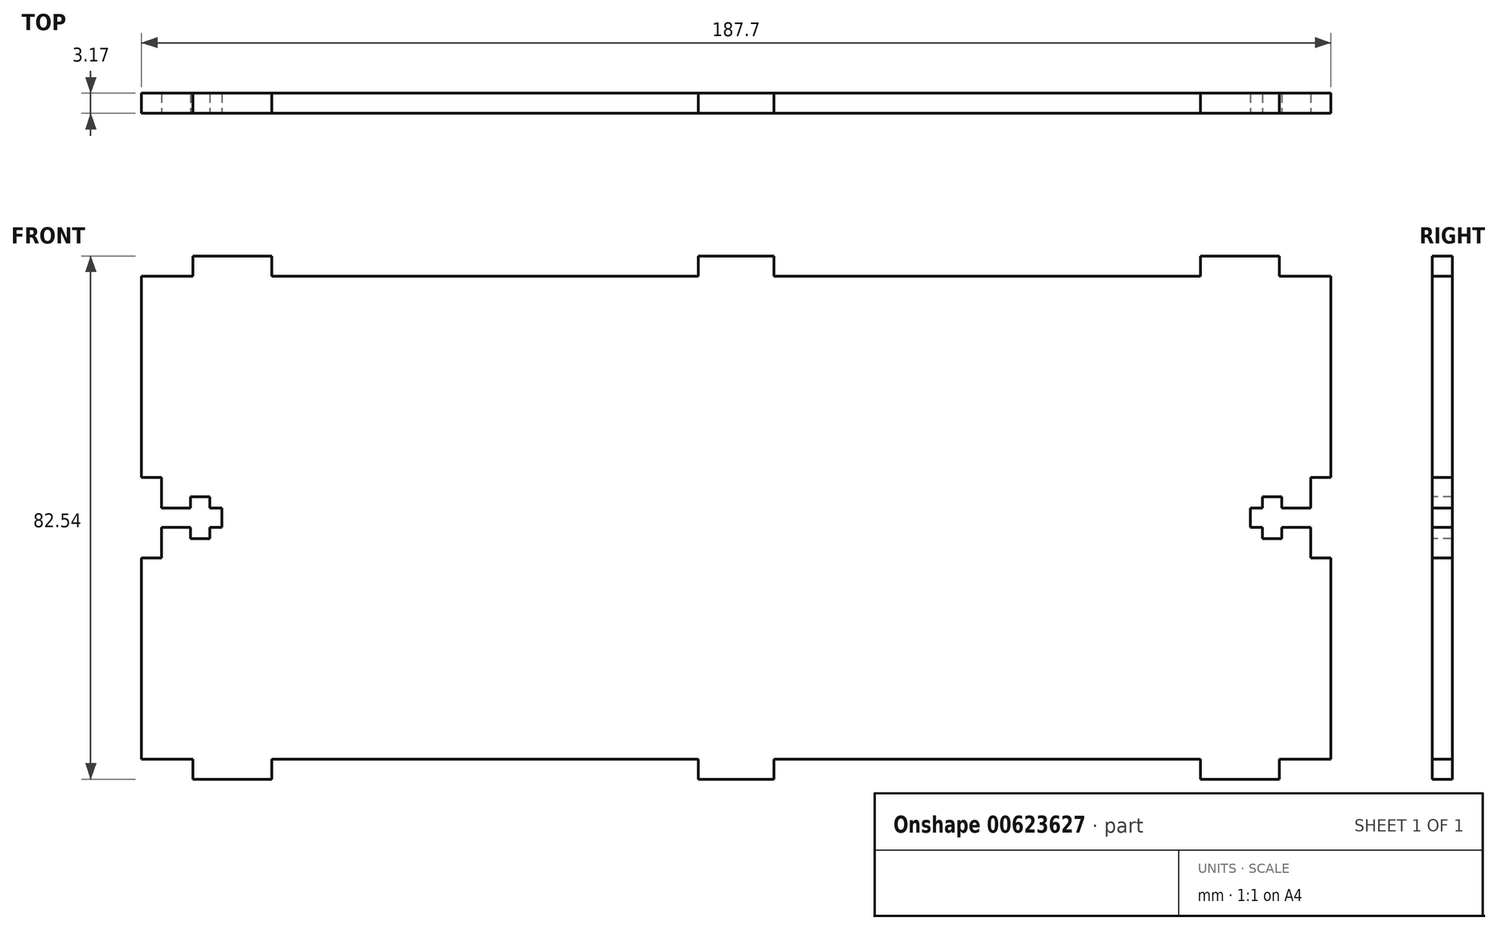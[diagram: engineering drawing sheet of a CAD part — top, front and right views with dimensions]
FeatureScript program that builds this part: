
annotation { "Feature Type Name" : "Feature", "Feature Type Description" : "" }
export const myFeature = defineFeature(function(context is Context, id is Id, definition is map)
    precondition{}
    {
        {
            var Q0;
            Q0=qCreatedBy(makeId("Front.planeOp"),FACE);
            var sketch = newSketch(context, id + "F0", { "sketchPlane" : qUnion([Q0])});
            skLineSegment(sketch, "E0.bottom", {"start": v(93.85, -41.27) * mm, "end": v(-93.85, -41.28) * mm});
            skLineSegment(sketch, "E0.top", {"start": v(93.85, 41.28) * mm, "end": v(-93.85, 41.27) * mm});
            skLineSegment(sketch, "E0.left", {"start": v(93.85, -41.27) * mm, "end": v(93.85, 41.28) * mm});
            skLineSegment(sketch, "E0.right", {"start": v(-93.85, -41.28) * mm, "end": v(-93.85, 41.27) * mm});
            skPoint(sketch, "E0.middle", {"position": v(0, 0) * mm});
            skSolve(sketch);
        }
        {
            var Q0;
            Q0 = qSketchRegion(id + "F0", true);
            extrude(context, id + "F1", {"entities" : qUnion([Q0]), "depth" : 3.17 * mm, "offsetDistance" : 25.4 * mm});
        }
        {
            var Q0;
            Q0=makeQuery(id+"F1.opExtrude","CAP_FACE",FACE,{"disambiguationData":[OSD([sQuery(id+"F0.wireOp",EDGE,"E0.bottom"),sQuery(id+"F0.wireOp",EDGE,"E0.top"),sQuery(id+"F0.wireOp",EDGE,"E0.left"),sQuery(id+"F0.wireOp",EDGE,"E0.right")])],"isStart":false});
            var sketch = newSketch(context, id + "F2", { "sketchPlane" : qUnion([Q0])});
            skLineSegment(sketch, "E1.bottom", {"start": v(-93.85, 41.27) * mm, "end": v(-85.73, 41.27) * mm});
            skLineSegment(sketch, "E1.top", {"start": v(-93.85, 38.1) * mm, "end": v(-85.73, 38.1) * mm});
            skLineSegment(sketch, "E1.left", {"start": v(-93.85, 41.27) * mm, "end": v(-93.85, 38.1) * mm});
            skLineSegment(sketch, "E1.right", {"start": v(-85.73, 41.27) * mm, "end": v(-85.73, 38.1) * mm});
            skLineSegment(sketch, "E2.bottom", {"start": v(-73.28, 41.27) * mm, "end": v(-5.97, 41.27) * mm});
            skLineSegment(sketch, "E2.top", {"start": v(-73.28, 38.1) * mm, "end": v(-5.97, 38.1) * mm});
            skLineSegment(sketch, "E2.left", {"start": v(-73.28, 41.27) * mm, "end": v(-73.28, 38.1) * mm});
            skLineSegment(sketch, "E2.right", {"start": v(-5.97, 41.27) * mm, "end": v(-5.97, 38.1) * mm});
            skLineSegment(sketch, "E3.MirrorCS", {"start": v(5.97, 41.27) * mm, "end": v(5.97, 38.1) * mm});
            skLineSegment(sketch, "E4.MirrorCS", {"start": v(93.85, 41.27) * mm, "end": v(93.85, 38.1) * mm});
            skLineSegment(sketch, "E5.MirrorCS", {"start": v(85.73, 41.27) * mm, "end": v(85.73, 38.1) * mm});
            skLineSegment(sketch, "E6.MirrorCS", {"start": v(73.28, 41.27) * mm, "end": v(73.28, 38.1) * mm});
            skLineSegment(sketch, "E7.MirrorCS", {"start": v(93.85, 41.27) * mm, "end": v(85.73, 41.27) * mm});
            skLineSegment(sketch, "E8.MirrorCS", {"start": v(93.85, 38.1) * mm, "end": v(85.73, 38.1) * mm});
            skLineSegment(sketch, "E9.MirrorCS", {"start": v(73.28, 41.27) * mm, "end": v(5.97, 41.27) * mm});
            skLineSegment(sketch, "E10.MirrorCS", {"start": v(73.28, 38.1) * mm, "end": v(5.97, 38.1) * mm});
            skLineSegment(sketch, "E11.MirrorCS", {"start": v(-73.28, -41.27) * mm, "end": v(-73.28, -38.1) * mm});
            skLineSegment(sketch, "E12.MirrorCS", {"start": v(-85.73, -41.27) * mm, "end": v(-85.73, -38.1) * mm});
            skLineSegment(sketch, "E13.MirrorCS", {"start": v(-93.85, -41.27) * mm, "end": v(-93.85, -38.1) * mm});
            skLineSegment(sketch, "E14.MirrorCS", {"start": v(73.28, -41.27) * mm, "end": v(73.28, -38.1) * mm});
            skLineSegment(sketch, "E15.MirrorCS", {"start": v(85.73, -41.27) * mm, "end": v(85.73, -38.1) * mm});
            skLineSegment(sketch, "E16.MirrorCS", {"start": v(93.85, -41.27) * mm, "end": v(93.85, -38.1) * mm});
            skLineSegment(sketch, "E17.MirrorCS", {"start": v(5.97, -41.27) * mm, "end": v(5.97, -38.1) * mm});
            skLineSegment(sketch, "E18.MirrorCS", {"start": v(-5.97, -41.27) * mm, "end": v(-5.97, -38.1) * mm});
            skLineSegment(sketch, "E19.MirrorCS", {"start": v(-73.28, -38.1) * mm, "end": v(-5.97, -38.1) * mm});
            skLineSegment(sketch, "E20.MirrorCS", {"start": v(-73.28, -41.27) * mm, "end": v(-5.97, -41.27) * mm});
            skLineSegment(sketch, "E21.MirrorCS", {"start": v(-93.85, -38.1) * mm, "end": v(-85.73, -38.1) * mm});
            skLineSegment(sketch, "E22.MirrorCS", {"start": v(-93.85, -41.27) * mm, "end": v(-85.73, -41.27) * mm});
            skLineSegment(sketch, "E23.MirrorCS", {"start": v(73.28, -41.27) * mm, "end": v(5.97, -41.27) * mm});
            skLineSegment(sketch, "E24.MirrorCS", {"start": v(73.28, -38.1) * mm, "end": v(5.97, -38.1) * mm});
            skLineSegment(sketch, "E25.MirrorCS", {"start": v(93.85, -41.27) * mm, "end": v(85.73, -41.27) * mm});
            skLineSegment(sketch, "E26.MirrorCS", {"start": v(93.85, -38.1) * mm, "end": v(85.73, -38.1) * mm});
            skLineSegment(sketch, "E27.bottom", {"start": v(-93.85, 6.35) * mm, "end": v(-90.68, 6.35) * mm});
            skLineSegment(sketch, "E27.top", {"start": v(-93.85, -6.35) * mm, "end": v(-90.68, -6.35) * mm});
            skLineSegment(sketch, "E27.left", {"start": v(-93.85, 6.35) * mm, "end": v(-93.85, -6.35) * mm});
            skLineSegment(sketch, "E27.right", {"start": v(-90.68, 6.35) * mm, "end": v(-90.68, 1.52) * mm});
            skLineSegment(sketch, "E28", {"start": v(-93.85, 0) * mm, "end": v(93.85, 0) * mm});
            skLineSegment(sketch, "E29.bottom", {"start": v(-90.68, 1.52) * mm, "end": v(-86.1, 1.52) * mm});
            skLineSegment(sketch, "E29.top", {"start": v(-90.68, -1.52) * mm, "end": v(-86.1, -1.52) * mm});
            skLineSegment(sketch, "E29.right", {"start": v(-81.15, 1.52) * mm, "end": v(-81.15, -1.52) * mm});
            skLineSegment(sketch, "E30.bottom", {"start": v(-86.1, 3.3) * mm, "end": v(-83.06, 3.3) * mm});
            skLineSegment(sketch, "E30.top", {"start": v(-86.1, -3.3) * mm, "end": v(-83.06, -3.3) * mm});
            skLineSegment(sketch, "E30.left", {"start": v(-86.1, 3.3) * mm, "end": v(-86.1, 1.52) * mm});
            skLineSegment(sketch, "E30.right", {"start": v(-83.06, 3.3) * mm, "end": v(-83.06, 1.52) * mm});
            skLineSegment(sketch, "E31.trimOffspring", {"start": v(-83.06, 1.52) * mm, "end": v(-81.15, 1.52) * mm});
            skLineSegment(sketch, "E32.trimOffspring", {"start": v(-86.1, -1.52) * mm, "end": v(-86.1, -3.3) * mm});
            skLineSegment(sketch, "E33.trimOffspring", {"start": v(-83.06, -1.52) * mm, "end": v(-83.06, -3.3) * mm});
            skLineSegment(sketch, "E34.trimOffspring", {"start": v(-90.68, -1.52) * mm, "end": v(-90.68, -6.35) * mm});
            skLineSegment(sketch, "E35.trimOffspring", {"start": v(-83.06, -1.52) * mm, "end": v(-81.15, -1.52) * mm});
            skLineSegment(sketch, "E36.MirrorCS", {"start": v(86.1, -1.52) * mm, "end": v(86.1, -3.3) * mm});
            skLineSegment(sketch, "E37.MirrorCS", {"start": v(93.85, 6.35) * mm, "end": v(90.68, 6.35) * mm});
            skLineSegment(sketch, "E38.MirrorCS", {"start": v(83.06, 3.3) * mm, "end": v(83.06, 1.52) * mm});
            skLineSegment(sketch, "E39.MirrorCS", {"start": v(86.1, -3.3) * mm, "end": v(83.06, -3.3) * mm});
            skLineSegment(sketch, "E40.MirrorCS", {"start": v(83.06, -1.52) * mm, "end": v(83.06, -3.3) * mm});
            skLineSegment(sketch, "E41.MirrorCS", {"start": v(93.85, -6.35) * mm, "end": v(90.68, -6.35) * mm});
            skLineSegment(sketch, "E42.MirrorCS", {"start": v(83.06, 1.52) * mm, "end": v(81.15, 1.52) * mm});
            skLineSegment(sketch, "E43.MirrorCS", {"start": v(86.1, 3.3) * mm, "end": v(83.06, 3.3) * mm});
            skLineSegment(sketch, "E44.MirrorCS", {"start": v(86.1, 3.3) * mm, "end": v(86.1, 1.52) * mm});
            skLineSegment(sketch, "E45.MirrorCS", {"start": v(83.06, -1.52) * mm, "end": v(81.15, -1.52) * mm});
            skLineSegment(sketch, "E46.MirrorCS", {"start": v(81.15, 1.52) * mm, "end": v(81.15, -1.52) * mm});
            skLineSegment(sketch, "E47.MirrorCS", {"start": v(93.85, 6.35) * mm, "end": v(93.85, -6.35) * mm});
            skLineSegment(sketch, "E48.MirrorCS", {"start": v(90.68, -1.52) * mm, "end": v(90.68, -6.35) * mm});
            skLineSegment(sketch, "E49.MirrorCS", {"start": v(90.68, -1.52) * mm, "end": v(86.1, -1.52) * mm});
            skLineSegment(sketch, "E50.MirrorCS", {"start": v(90.68, 6.35) * mm, "end": v(90.68, 1.52) * mm});
            skLineSegment(sketch, "E51.MirrorCS", {"start": v(90.68, 1.52) * mm, "end": v(86.1, 1.52) * mm});
            skSolve(sketch);
        }
        {
            var Q0;
            Q0 = qSketchRegion(id + "F2", true);
            extrude(context, id + "F3", {"entities" : qUnion([Q0]), "operationType" : NewBodyOperationType.REMOVE, "oppositeDirection" : true, "depth" : 3.17 * mm, "offsetDistance" : 25.4 * mm});
        }
    });
